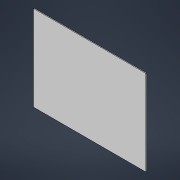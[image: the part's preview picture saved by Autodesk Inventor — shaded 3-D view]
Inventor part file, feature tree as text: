
AUTODESK INVENTOR PART (.ipt)
format: ipt  version: 2022 (Build 260153070, 153G)  size: 108,544 bytes
history: native  units: mm
features: other x1, sketch x1, extrude x1, chamfer x1
ambient origin geometry x8: Origin, YZ Plane, XZ Plane, XY Plane, X Axis, Y Axis, Z Axis, Center Point
bodies: Body1 (feature_tree)
feature tree (4):
  other  "Твердое тело1"
  sketch  "Эскиз1"
  extrude  "Выдавливание1"  Depth=218.0mm
  chamfer  "Фаска1"  Distance=166.0mm
